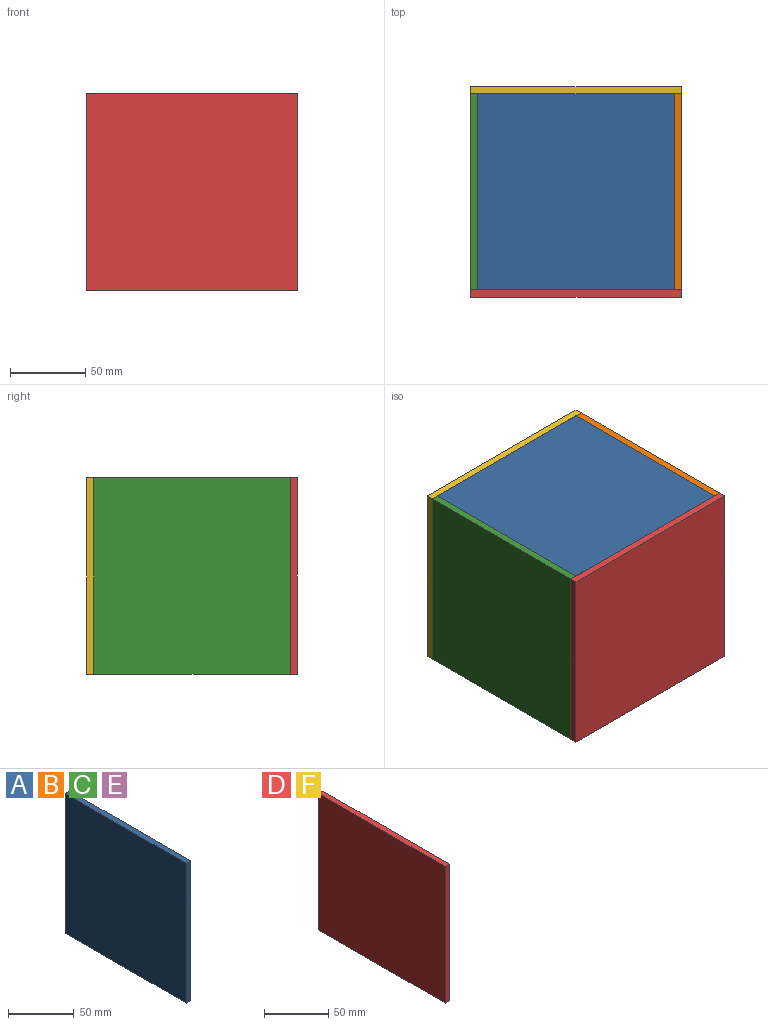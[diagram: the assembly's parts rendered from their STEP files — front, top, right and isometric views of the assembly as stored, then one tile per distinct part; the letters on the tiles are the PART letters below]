
ASSEMBLY  parts=6 mates=15
PART A: 6 faces, bbox 4.8x130.2x130.2 mm
  f0: plane 130.18x4.76mm, normal (0,0,1), area 620mm2, adj f1,f3,f4,f5
  f1: plane 130.18x4.76mm, normal (0,-1,0), area 620mm2, adj f0,f2,f4,f5
  f2: plane 130.18x4.76mm, normal (0,0,-1), area 620mm2, adj f1,f3,f4,f5
  f3: plane 130.18x4.76mm, normal (0,1,0), area 620mm2, adj f0,f2,f4,f5
  f4: plane 130.18x130.18mm, normal (1,0,0), area 16945.5mm2, adj f0,f1,f2,f3
  f5: plane 130.18x130.18mm, normal (-1,0,0), area 16945.5mm2, adj f0,f1,f2,f3
PART B: same geometry as A
PART C: same geometry as A
PART D: 6 faces, bbox 4.8x139.7x130.2 mm
  f0: plane 139.7x4.76mm, normal (0,0,1), area 665.3mm2, adj f1,f3,f4,f5
  f1: plane 130.18x4.76mm, normal (0,-1,0), area 620mm2, adj f0,f2,f4,f5
  f2: plane 139.7x4.76mm, normal (0,0,-1), area 665.3mm2, adj f1,f3,f4,f5
  f3: plane 130.18x4.76mm, normal (0,1,0), area 620mm2, adj f0,f2,f4,f5
  f4: plane 139.7x130.18mm, normal (1,0,0), area 18185.4mm2, adj f0,f1,f2,f3
  f5: plane 139.7x130.18mm, normal (-1,0,0), area 18185.4mm2, adj f0,f1,f2,f3
PART E: same geometry as A
PART F: same geometry as D
PLACE A rot(axis=(0,1,0),90deg) t=(-3.99,-0.35,73.53)mm
PLACE B rot(axis=(0,0,1),180deg) t=(65.86,-0.35,8.44)mm
PLACE C t=(-73.84,-0.35,8.44)mm
PLACE D rot(axis=(0,0,-1),90deg) t=(-3.99,-65.44,8.44)mm
PLACE E rot(axis=(-0.58,0.58,0.58),120deg) t=(-3.99,-0.35,-51.88)mm
PLACE F rot(axis=(0,0,-1),90deg) t=(-3.99,69.5,8.44)mm
MATE planar A.f5 <-> C.f0  axis (0,0,1) through (-3.99,-0.35,73.53)mm
MATE planar B.f2 <-> E.f4  axis (0,0,-1) through (63.48,-0.35,-56.64)mm
MATE planar D.f5 <-> C.f1  axis (0,1,0) through (-3.99,-65.44,8.44)mm
MATE planar E.f3 <-> C.f4  axis (-1,0,0) through (-69.08,-0.35,-54.26)mm
MATE planar F.f1 <-> C.f5  axis (-1,0,0) through (-73.84,67.12,8.44)mm
MATE planar B.f4 <-> A.f0  axis (-1,0,0) through (61.1,-0.35,8.44)mm
MATE planar B.f1 <-> E.f0  axis (0,1,0) through (63.48,64.74,8.44)mm
MATE planar A.f3 <-> B.f1  axis (0,1,0) through (-3.99,64.74,71.15)mm
MATE planar C.f3 <-> F.f4  axis (0,1,0) through (-71.46,64.74,73.53)mm
MATE planar B.f5 <-> D.f3  axis (1,0,0) through (65.86,-0.35,8.44)mm
MATE planar B.f4 <-> E.f1  axis (-1,0,0) through (61.1,-0.35,8.44)mm
MATE planar C.f3 <-> A.f3  axis (0,1,0) through (-71.46,64.74,8.44)mm
MATE planar F.f0 <-> A.f5  axis (0,0,1) through (-3.99,67.12,73.53)mm
MATE planar D.f2 <-> E.f4  axis (0,0,-1) through (-3.99,-67.82,-56.64)mm
MATE planar E.f4 <-> C.f2  axis (0,0,-1) through (-3.99,-0.35,-56.64)mm
